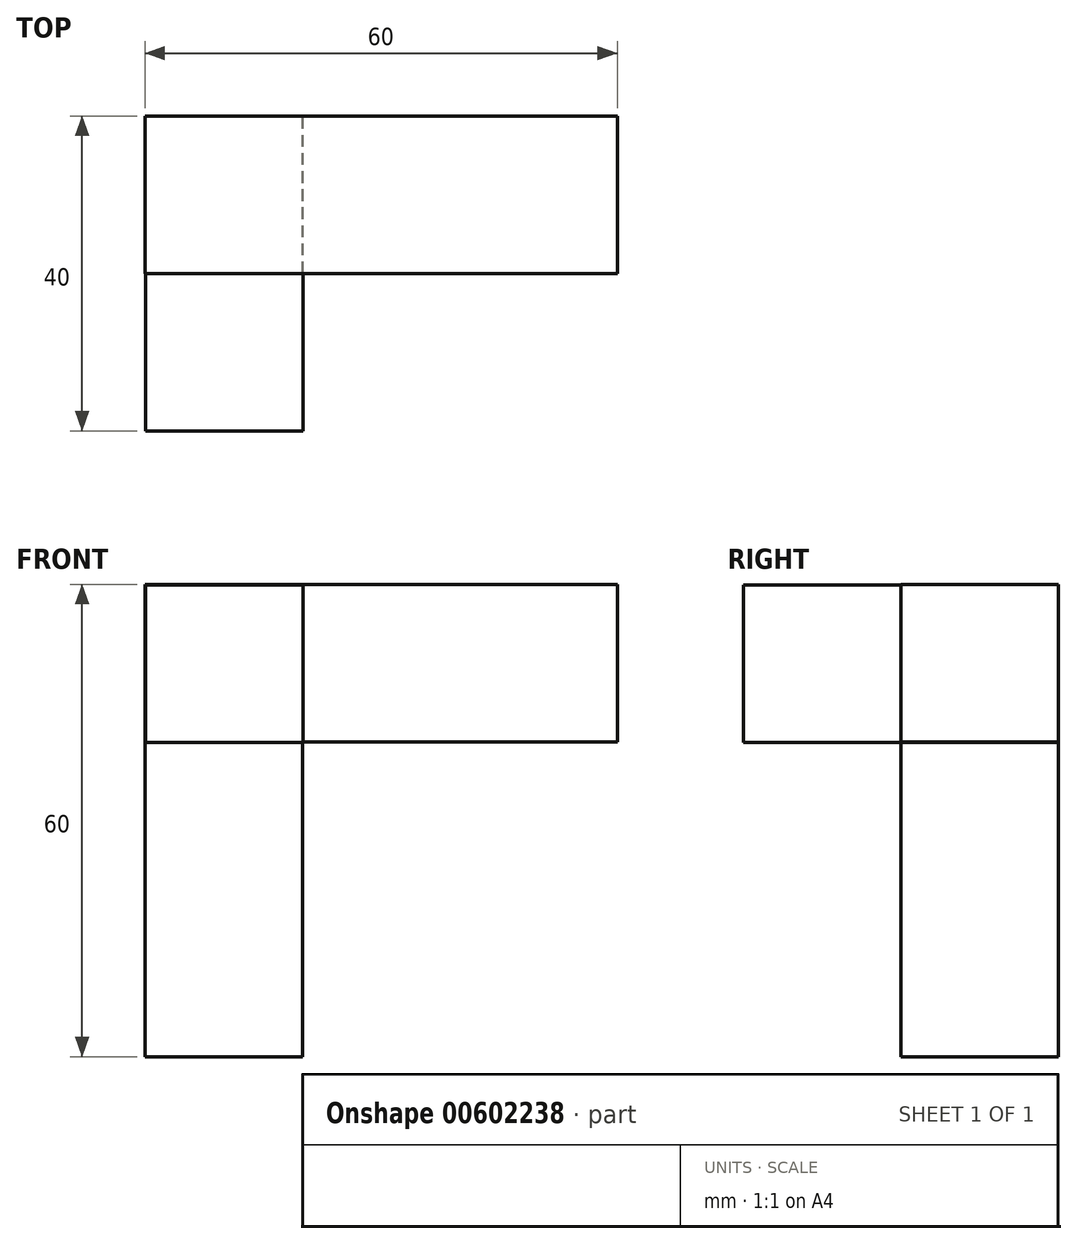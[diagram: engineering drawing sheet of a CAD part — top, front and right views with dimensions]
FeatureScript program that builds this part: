
annotation { "Feature Type Name" : "Feature", "Feature Type Description" : "" }
export const myFeature = defineFeature(function(context is Context, id is Id, definition is map)
    precondition{}
    {
        {
            var Q0;
            Q0=qCreatedBy(makeId("Front.planeOp"),FACE);
            var sketch = newSketch(context, id + "F0", { "sketchPlane" : qUnion([Q0])});
            skLineSegment(sketch, "E0", {"start": v(-47.85, 67.52) * mm, "end": v(-47.85, 7.52) * mm});
            skLineSegment(sketch, "E1", {"start": v(-47.85, 67.52) * mm, "end": v(12.15, 67.52) * mm});
            skPoint(sketch, "E2.endSnap0", {"position": v(-47.85, 37.52) * mm});
            skLineSegment(sketch, "E3", {"start": v(-47.85, 7.52) * mm, "end": v(-27.85, 7.52) * mm});
            skLineSegment(sketch, "E4", {"start": v(-27.85, 47.52) * mm, "end": v(-27.85, 7.52) * mm});
            skLineSegment(sketch, "E5", {"start": v(-27.85, 47.52) * mm, "end": v(12.15, 47.52) * mm});
            skLineSegment(sketch, "E6", {"start": v(12.15, 47.52) * mm, "end": v(12.15, 67.52) * mm});
            skSolve(sketch);
        }
        {
            var Q0;
            Q0 = qSketchRegion(id + "F0", true);
            extrude(context, id + "F1", {"entities" : qUnion([Q0]), "depth" : 20 * mm, "offsetDistance" : 25 * mm});
        }
        {
            var Q0;
            Q0=qCreatedBy(makeId("Front.planeOp"),FACE);
            var sketch = newSketch(context, id + "F2", { "sketchPlane" : qUnion([Q0])});
            skLineSegment(sketch, "E7", {"start": v(-47.8, 67.45) * mm, "end": v(-27.8, 67.45) * mm});
            skLineSegment(sketch, "E8", {"start": v(-27.8, 67.45) * mm, "end": v(-27.8, 47.45) * mm});
            skLineSegment(sketch, "E9", {"start": v(-27.8, 47.45) * mm, "end": v(-47.8, 47.45) * mm});
            skLineSegment(sketch, "E10", {"start": v(-47.8, 47.45) * mm, "end": v(-47.8, 67.45) * mm});
            skSolve(sketch);
        }
        {
            var Q0;
            Q0 = qSketchRegion(id + "F2", true);
            extrude(context, id + "F3", {"entities" : qUnion([Q0]), "operationType" : NewBodyOperationType.ADD, "depth" : 40 * mm, "offsetDistance" : 25 * mm});
        }
    });
